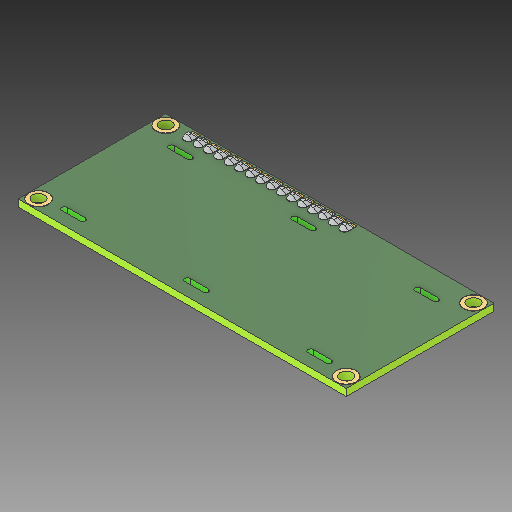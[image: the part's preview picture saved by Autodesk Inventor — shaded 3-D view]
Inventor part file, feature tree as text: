
AUTODESK INVENTOR PART (.ipt)
format: ipt  version: 2019 (Build 230136000, 136)  size: 792,576 bytes
history: mixed  units: in
note: dims shown in document units (in); Inventor stores cm internally (conversion verified against a paired STEP export)
features: fillet x1, imported_body x1
ambient origin geometry x8: Origin, YZ Plane, XZ Plane, XY Plane, X Axis, Y Axis, Z Axis, Center Point
bodies: Solid1 (imported_parasolid)
feature tree (2):
  fillet  "Fillet6"  [1 undecoded]
  imported_body  NMx_Import_Brep_tag  [imported B-rep: ~21 faces, bbox_mm=[79.75, 0.05, 36.0]]
note: 1 required parameter value undecoded (feature->parameter linkage not recoverable at this tier; creation-order binding heuristic only, values carry confidence <= 0.55)
